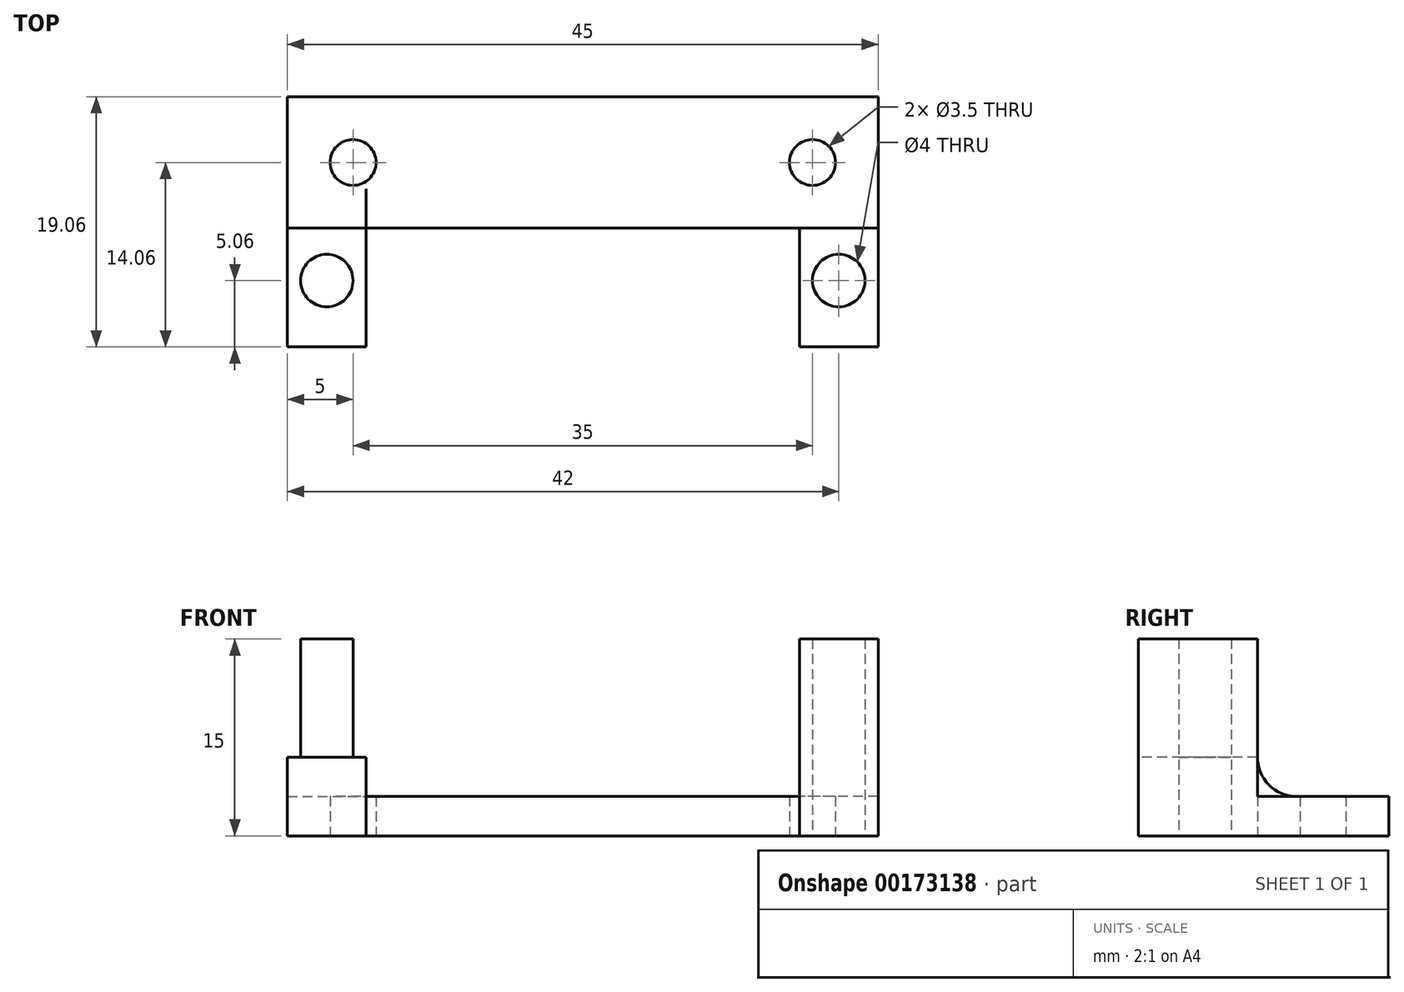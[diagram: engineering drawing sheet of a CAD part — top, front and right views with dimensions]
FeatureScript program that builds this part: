
annotation { "Feature Type Name" : "Feature", "Feature Type Description" : "" }
export const myFeature = defineFeature(function(context is Context, id is Id, definition is map)
    precondition{}
    {
        {
            var Q0;
            Q0=qCreatedBy(makeId("Top.planeOp"),FACE);
            var sketch = newSketch(context, id + "F0", { "sketchPlane" : qUnion([Q0])});
            skLineSegment(sketch, "E0.bottom", {"start": v(-22.5, 5) * mm, "end": v(22.5, 5) * mm});
            skLineSegment(sketch, "E0.top", {"start": v(-16.5, -5) * mm, "end": v(22.5, -5) * mm});
            skPoint(sketch, "E1", {"position": v(-17.5, 0) * mm});
            skPoint(sketch, "E2.MirrorP", {"position": v(17.5, 0) * mm});
            skLineSegment(sketch, "E3", {"start": v(-22.5, -14.06) * mm, "end": v(-16.5, -14.06) * mm});
            skLineSegment(sketch, "E4", {"start": v(-16.5, -14.06) * mm, "end": v(-16.5, -5) * mm});
            skLineSegment(sketch, "E5", {"start": v(-22.5, 5) * mm, "end": v(-22.5, -14.06) * mm});
            skPoint(sketch, "E6", {"position": v(-19.5, -9) * mm});
            skPoint(sketch, "E7", {"position": v(-19.5, -14.06) * mm});
            skCircle(sketch, "E8", {"center": v(-19.5, -9) * mm, "radius": 2 * mm});
            skLineSegment(sketch, "E9", {"start": v(-16.5, -5) * mm, "end": v(-22.5, -5) * mm});
            skLineSegment(sketch, "E10.MirrorCS", {"start": v(22.5, -14.06) * mm, "end": v(16.5, -14.06) * mm});
            skLineSegment(sketch, "E11.MirrorCS", {"start": v(16.5, -14.06) * mm, "end": v(16.5, -5) * mm});
            skCircle(sketch, "E12.MirrorC", {"center": v(19.5, -9) * mm, "radius": 2 * mm});
            skLineSegment(sketch, "E13.MirrorCS", {"start": v(22.5, 5) * mm, "end": v(22.5, -14.06) * mm});
            skSolve(sketch);
        }
        {
            var Q0;
            {var subQ4=sQuery(id+"F0.wireOp",EDGE,"E0.top");Q0=makeQuery(id+"F0.imprint","IMPRINT",FACE,{"disambiguationData":[TD([[makeQuery(id+"F0.imprint","IMPRINT",EDGE,{"derivedFrom":subQ4}),1.0]])]});}
            var Q1;
            {var subQ0=sQuery(id+"F0.wireOp",EDGE,"OXRn6v1C-EZUR-LP8s-jIyZ-FZDUjvtOetUh");Q1=makeQuery(id+"F0.imprint","IMPRINT",FACE,{"disambiguationData":[TD([[makeQuery(id+"F0.imprint","IMPRINT",EDGE,{"derivedFrom":subQ0}),-1.0]])]});}
            var Q2;
            {var subQ11=sQuery(id+"F0.wireOp",EDGE,"7J2wvqM4-xPlB-OBpe-c7Rh-MZsjYVVmt19z.bottom");Q2=makeQuery(id+"F0.imprint","IMPRINT",FACE,{"disambiguationData":[TD([[makeQuery(id+"F0.imprint","IMPRINT",EDGE,{"derivedFrom":subQ11}),-1.0]])]});}
            var Q3;
            Q3=makeQuery(id+"F0.imprint","IMPRINT",FACE,{"disambiguationData":[TD([[makeQuery(id+"F0.imprint","IMPRINT",EDGE,{"derivedFrom":sQuery(id+"F0.wireOp",EDGE,"7J2wvqM4-xPlB-OBpe-c7Rh-MZsjYVVmt19z.bottom")}),1.0]])]});
            var Q4;
            {var subQ4=sQuery(id+"F0.wireOp",EDGE,"d9b5b526-6597-48c5-ab9b-9fa32d05a7710.MirrorCS");Q4=makeQuery(id+"F0.imprint","IMPRINT",FACE,{"disambiguationData":[TD([[makeQuery(id+"F0.imprint","IMPRINT",EDGE,{"derivedFrom":subQ4}),-1.0]])]});}
            var Q5;
            {var subQ0=sQuery(id+"F0.wireOp",EDGE,"1JvEsqPi-Z3tJ-0mLx-tlPS-sn2HiT6P478m");var subQ1=makeQuery(id+"F0.imprint","INTERSECT",VERTEX,{"derivedFrom":[subQ0,sQuery(id+"F0.wireOp",EDGE,"1c222ab1-99cf-4a52-b06c-a2d144bff72d.trimOffspring")]});Q5=makeQuery(id+"F0.imprint","IMPRINT",FACE,{"disambiguationData":[TD([[makeQuery(id+"F0.imprint","IMPRINT",EDGE,{"disambiguationData":[TD([[subQ1,-1.0]])],"derivedFrom":subQ0}),1.0]])]});}
            var Q6;
            {var subQ0=sQuery(id+"F0.wireOp",EDGE,"623a4435-3ed8-4d58-b833-2add5df1d3c10.MirrorC");var subQ1=makeQuery(id+"F0.imprint","INTERSECT",VERTEX,{"derivedFrom":[subQ0,sQuery(id+"F0.wireOp",EDGE,"1527e2e3-68ff-4f82-bfa2-71ee807c68ce.trimOffspring")]});Q6=makeQuery(id+"F0.imprint","IMPRINT",FACE,{"disambiguationData":[TD([[makeQuery(id+"F0.imprint","IMPRINT",EDGE,{"disambiguationData":[TD([[subQ1,1.0]])],"derivedFrom":subQ0}),-1.0]])]});}
            var Q7;
            {var subQ3=sQuery(id+"F0.wireOp",EDGE,"a21e8333-434e-4f72-96e8-9f9a5c8b278a.trimOffspring");Q7=makeQuery(id+"F0.imprint","IMPRINT",FACE,{"disambiguationData":[TD([[makeQuery(id+"F0.imprint","IMPRINT",EDGE,{"derivedFrom":subQ3}),-1.0]])]});}
            var Q8;
            {var subQ0=sQuery(id+"F0.wireOp",EDGE,"cdd2d55c-9578-41ba-93dc-552cf4d5b990.trimOffspring");Q8=makeQuery(id+"F0.imprint","IMPRINT",FACE,{"disambiguationData":[TD([[makeQuery(id+"F0.imprint","IMPRINT",EDGE,{"derivedFrom":subQ0}),1.0]])]});}
            var Q9;
            {var subQ2=sQuery(id+"F0.wireOp",EDGE,"HOqkVMfu-S4OV-G5Dd-tlBz-ib7erGi4niXI");var subQ5=sQuery(id+"F0.wireOp",EDGE,"FVEzBznb-eyU1-3iTB-GpGh-xkmCeVU1Wi0z");var subQ6=makeQuery(id+"F0.imprint","INTERSECT",VERTEX,{"disambiguationData":[OD(0.0)],"derivedFrom":[subQ5,subQ2]});Q9=makeQuery(id+"F0.imprint","IMPRINT",FACE,{"disambiguationData":[TD([[makeQuery(id+"F0.imprint","IMPRINT",EDGE,{"disambiguationData":[TD([[subQ6,1.0]])],"derivedFrom":subQ5}),-1.0]])]});}
            var Q10;
            {var subQ3=sQuery(id+"F0.wireOp",EDGE,"HOqkVMfu-S4OV-G5Dd-tlBz-ib7erGi4niXI");var subQ6=sQuery(id+"F0.wireOp",EDGE,"209e6423-f482-4120-8dec-f25d50a8a9110.MirrorC");var subQ7=makeQuery(id+"F0.imprint","INTERSECT",VERTEX,{"disambiguationData":[OD(0.0)],"derivedFrom":[subQ6,subQ3]});Q10=makeQuery(id+"F0.imprint","IMPRINT",FACE,{"disambiguationData":[TD([[makeQuery(id+"F0.imprint","IMPRINT",EDGE,{"disambiguationData":[TD([[subQ7,-1.0]])],"derivedFrom":subQ6}),1.0]])]});}
            var Q11;
            {var subQ3=sQuery(id+"F0.wireOp",EDGE,"b3270a8a-f979-498d-b00d-41179a4714080.MirrorCS");Q11=makeQuery(id+"F0.imprint","IMPRINT",FACE,{"disambiguationData":[TD([[makeQuery(id+"F0.imprint","IMPRINT",EDGE,{"derivedFrom":subQ3}),-1.0]])]});}
            var Q12;
            {var subQ0=sQuery(id+"F0.wireOp",EDGE,"bfbb188b-f2e7-4029-96ce-91e3871fe3b6.trimOffspring");Q12=makeQuery(id+"F0.imprint","IMPRINT",FACE,{"disambiguationData":[TD([[makeQuery(id+"F0.imprint","IMPRINT",EDGE,{"derivedFrom":subQ0}),-1.0]])]});}
            var Q13;
            {var subQ0=sQuery(id+"F0.wireOp",EDGE,"VjLgxMTG-fYXR-nb2F-9DFL-ZEoaj6BwpKOL");Q13=makeQuery(id+"F0.imprint","IMPRINT",FACE,{"disambiguationData":[TD([[makeQuery(id+"F0.imprint","IMPRINT",EDGE,{"derivedFrom":subQ0}),-1.0]])]});}
            var Q14;
            {var subQ0=sQuery(id+"F0.wireOp",EDGE,"03e3ae5e-7516-4045-97f7-42c8b8d69dca0.MirrorCS");Q14=makeQuery(id+"F0.imprint","IMPRINT",FACE,{"disambiguationData":[TD([[makeQuery(id+"F0.imprint","IMPRINT",EDGE,{"derivedFrom":subQ0}),1.0]])]});}
            var Q15;
            {var subQ0=sQuery(id+"F0.wireOp",EDGE,"1527e2e3-68ff-4f82-bfa2-71ee807c68ce.trimOffspring");Q15=makeQuery(id+"F0.imprint","IMPRINT",FACE,{"disambiguationData":[TD([[makeQuery(id+"F0.imprint","IMPRINT",EDGE,{"derivedFrom":subQ0}),-1.0]])]});}
            var Q16;
            Q16=makeQuery(id+"F0.imprint","IMPRINT",FACE,{"disambiguationData":[TD([[makeQuery(id+"F0.imprint","IMPRINT",EDGE,{"derivedFrom":sQuery(id+"F0.wireOp",EDGE,"E8")}),1.0]])]});
            var Q17;
            {var subQ1=sQuery(id+"F0.wireOp",EDGE,"E3");Q17=makeQuery(id+"F0.imprint","IMPRINT",FACE,{"disambiguationData":[TD([[makeQuery(id+"F0.imprint","IMPRINT",EDGE,{"derivedFrom":subQ1}),1.0]])]});}
            var Q18;
            Q18=makeQuery(id+"F0.imprint","IMPRINT",FACE,{"disambiguationData":[TD([[makeQuery(id+"F0.imprint","IMPRINT",EDGE,{"derivedFrom":sQuery(id+"F0.wireOp",EDGE,"E12.MirrorC")}),-1.0]])]});
            var Q19;
            {var subQ1=sQuery(id+"F0.wireOp",EDGE,"E10.MirrorCS");Q19=makeQuery(id+"F0.imprint","IMPRINT",FACE,{"disambiguationData":[TD([[makeQuery(id+"F0.imprint","IMPRINT",EDGE,{"derivedFrom":subQ1}),-1.0]])]});}
            extrude(context, id + "F1", {"entities" : qUnion([Q0, Q1, Q2, Q3, Q4, Q5, Q6, Q7, Q8, Q9, Q10, Q11, Q12, Q13, Q14, Q15, Q16, Q17, Q18, Q19]), "depth" : 3 * mm});
        }
        {
            var Q0;
            Q0=sQuery(id+"F0.wireOp",VERTEX,"E1");
            var Q1;
            Q1=sQuery(id+"F0.wireOp",VERTEX,"E2.MirrorP");
            var Q2;
            Q2=makeQuery(id+"F1.opExtrude","SWEPT_BODY",BODY,{"disambiguationData":[OSD([sQuery(id+"F0.wireOp",EDGE,"E0.top"),sQuery(id+"F0.wireOp",EDGE,"E0.right"),sQuery(id+"F0.wireOp",EDGE,"E0.bottom"),sQuery(id+"F0.wireOp",EDGE,"E3"),sQuery(id+"F0.wireOp",EDGE,"E4"),sQuery(id+"F0.wireOp",EDGE,"E5")])]});
            hole(context, id + "F2", {"style" : HoleStyle.SIMPLE, "endStyle" : HoleEndStyle.THROUGH, "oppositeDirection" : true, "holeDiameter" : 3.5 * mm, "startFromSketch" : true, "locations" : qUnion([Q0, Q1]), "scope" : qUnion([Q2]), "isTappedThrough" : true});
        }
        {
            var Q0;
            Q0=makeQuery(id+"F0.imprint","IMPRINT",FACE,{"disambiguationData":[TD([[makeQuery(id+"F0.imprint","IMPRINT",EDGE,{"derivedFrom":sQuery(id+"F0.wireOp",EDGE,"E8")}),1.0]])]});
            var Q1;
            Q1=makeQuery(id+"F0.imprint","IMPRINT",FACE,{"disambiguationData":[TD([[makeQuery(id+"F0.imprint","IMPRINT",EDGE,{"derivedFrom":sQuery(id+"F0.wireOp",EDGE,"E12.MirrorC")}),-1.0]])]});
            extrude(context, id + "F3", {"entities" : qUnion([Q0, Q1]), "operationType" : NewBodyOperationType.ADD, "depth" : 15 * mm});
        }
        {
            var Q0;
            Q0=makeQuery(id+"F0.imprint","IMPRINT",FACE,{"disambiguationData":[TD([[makeQuery(id+"F0.imprint","IMPRINT",EDGE,{"derivedFrom":sQuery(id+"F0.wireOp",EDGE,"E8")}),1.0]])]});
            var Q1;
            {var subQ1=sQuery(id+"F0.wireOp",EDGE,"E3");Q1=makeQuery(id+"F0.imprint","IMPRINT",FACE,{"disambiguationData":[TD([[makeQuery(id+"F0.imprint","IMPRINT",EDGE,{"derivedFrom":subQ1}),1.0]])]});}
            var Q2;
            {var subQ1=sQuery(id+"F0.wireOp",EDGE,"E10.MirrorCS");Q2=makeQuery(id+"F0.imprint","IMPRINT",FACE,{"disambiguationData":[TD([[makeQuery(id+"F0.imprint","IMPRINT",EDGE,{"derivedFrom":subQ1}),-1.0]])]});}
            extrude(context, id + "F4", {"entities" : qUnion([Q0, Q1, Q2]), "operationType" : NewBodyOperationType.ADD, "depth" : 6 * mm});
        }
        {
            var Q0;
            Q0=makeQuery(id+"F4.boolean.opBoolean","INTERSECT",EDGE,{"derivedFrom":[makeQuery(id+"F1.opExtrude","CAP_FACE",FACE,{"disambiguationData":[OSD([sQuery(id+"F0.wireOp",EDGE,"E0.top"),sQuery(id+"F0.wireOp",EDGE,"E0.right"),sQuery(id+"F0.wireOp",EDGE,"E0.bottom"),sQuery(id+"F0.wireOp",EDGE,"E3"),sQuery(id+"F0.wireOp",EDGE,"E4"),sQuery(id+"F0.wireOp",EDGE,"E5")])],"isStart":false}),makeQuery(id+"F4.opExtrude","SWEPT_FACE",FACE,{"disambiguationData":[OSD([sQuery(id+"F0.wireOp",EDGE,"E9")])]})]});
            var Q1;
            {var subQ0=sQuery(id+"F0.wireOp",EDGE,"E0.top");Q1=makeQuery(id+"F4.boolean.opBoolean","INTERSECT",EDGE,{"derivedFrom":[makeQuery(id+"F1.opExtrude","CAP_FACE",FACE,{"disambiguationData":[OSD([subQ0,sQuery(id+"F0.wireOp",EDGE,"E0.bottom"),sQuery(id+"F0.wireOp",EDGE,"E3"),sQuery(id+"F0.wireOp",EDGE,"E4"),sQuery(id+"F0.wireOp",EDGE,"E5"),sQuery(id+"F0.wireOp",EDGE,"E10.MirrorCS"),sQuery(id+"F0.wireOp",EDGE,"E11.MirrorCS"),sQuery(id+"F0.wireOp",EDGE,"E13.MirrorCS")])],"isStart":false}),makeQuery(id+"F4.opExtrude","SWEPT_FACE",FACE,{"disambiguationData":[OSD([subQ0])]})]});}
            fillet(context, id + "F5", {"entities" : qUnion([Q0, Q1]), "radius" : 3 * mm, "tangentPropagation" : true, "allowEdgeOverflow" : false});
        }
    });
